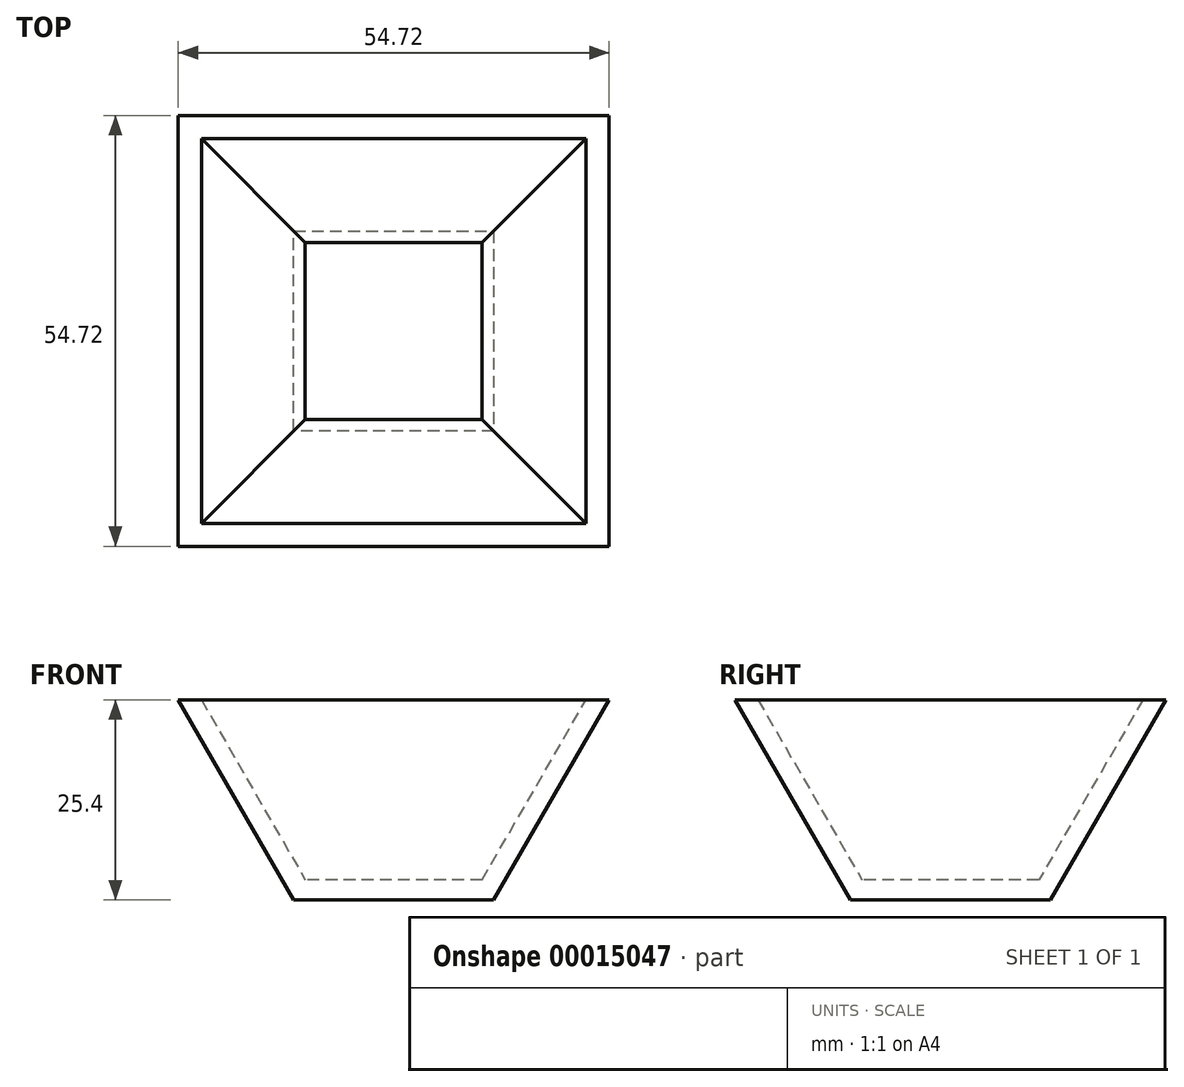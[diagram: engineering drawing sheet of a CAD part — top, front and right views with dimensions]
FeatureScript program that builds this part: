
annotation { "Feature Type Name" : "Feature", "Feature Type Description" : "" }
export const myFeature = defineFeature(function(context is Context, id is Id, definition is map)
    precondition{}
    {
        {
            var Q0;
            Q0=qCreatedBy(makeId("Top.planeOp"),FACE);
            var sketch = newSketch(context, id + "F0", { "sketchPlane" : qUnion([Q0])});
            skLineSegment(sketch, "E0.bottom", {"start": v(12.7, -12.7) * mm, "end": v(-12.7, -12.7) * mm});
            skLineSegment(sketch, "E0.top", {"start": v(12.7, 12.7) * mm, "end": v(-12.7, 12.7) * mm});
            skLineSegment(sketch, "E0.left", {"start": v(12.7, -12.7) * mm, "end": v(12.7, 12.7) * mm});
            skLineSegment(sketch, "E0.right", {"start": v(-12.7, -12.7) * mm, "end": v(-12.7, 12.7) * mm});
            skPoint(sketch, "E0.middle", {"position": v(0, 0) * mm});
            skSolve(sketch);
        }
        {
            var Q0;
            Q0 = qSketchRegion(id + "F0", true);
            extrude(context, id + "F1", {"entities" : qUnion([Q0]), "depth" : 25.4 * mm, "hasDraft" : true, "draftAngle" : 30 * degree});
        }
        {
            var Q0;
            Q0=makeQuery(id+"F1.opExtrude","CAP_FACE",FACE,{"disambiguationData":[OSD([sQuery(id+"F0.wireOp",EDGE,"E0.bottom"),sQuery(id+"F0.wireOp",EDGE,"E0.top"),sQuery(id+"F0.wireOp",EDGE,"E0.left"),sQuery(id+"F0.wireOp",EDGE,"E0.right")])],"isStart":false});
            shell(context, id + "F2", {"entities" : qUnion([Q0]), "thickness" : 2.54 * mm});
        }
    });
